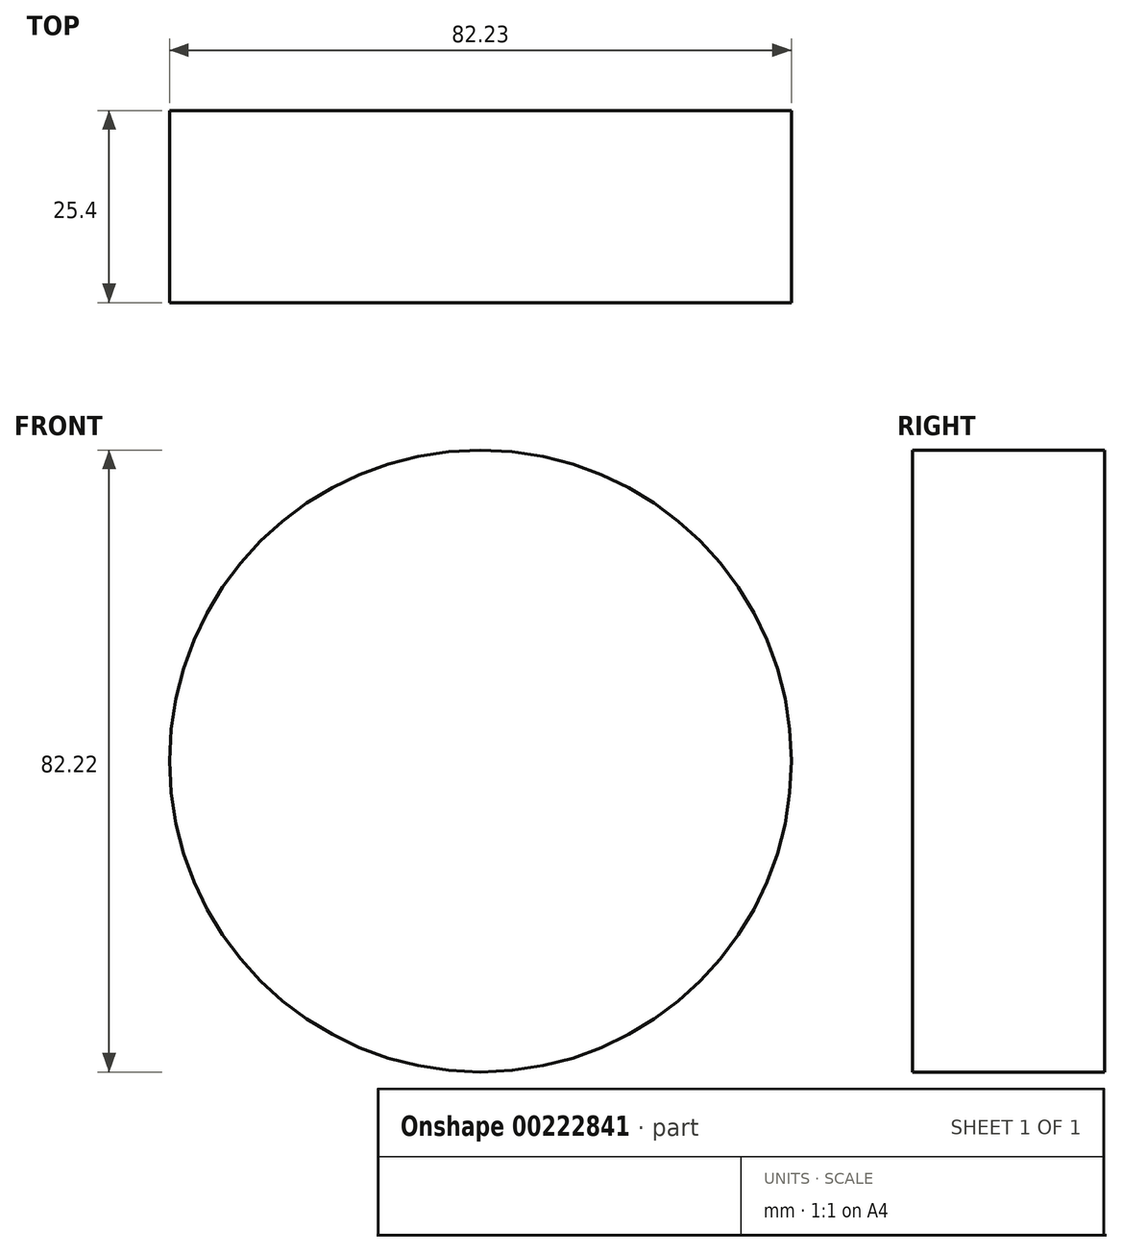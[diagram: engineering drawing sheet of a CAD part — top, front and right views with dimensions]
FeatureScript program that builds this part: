
annotation { "Feature Type Name" : "Feature", "Feature Type Description" : "" }
export const myFeature = defineFeature(function(context is Context, id is Id, definition is map)
    precondition{}
    {
        {
            var Q0;
            Q0=qCreatedBy(makeId("Front.planeOp"),FACE);
            var sketch = newSketch(context, id + "F0", { "sketchPlane" : qUnion([Q0])});
            skCircle(sketch, "E0", {"center": v(17.37, -8.53) * mm, "radius": 41.11 * mm});
            skSolve(sketch);
        }
        {
            var Q0;
            Q0=makeQuery(id+"F0.imprint","IMPRINT",FACE,{"disambiguationData":[TD([[makeQuery(id+"F0.imprint","IMPRINT",EDGE,{"derivedFrom":sQuery(id+"F0.wireOp",EDGE,"E0")}),1.0]])]});
            extrude(context, id + "F1", {"entities" : qUnion([Q0]), "depth" : 25.4 * mm});
        }
    });
